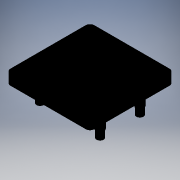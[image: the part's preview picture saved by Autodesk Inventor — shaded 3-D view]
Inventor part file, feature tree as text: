
AUTODESK INVENTOR PART (.ipt)
format: ipt  version: 2017.3 (Build 213256000, 256)  size: 133,632 bytes
history: native  units: mm (DEFAULTED — no unit token found)
features: other x7, sketch x3, extrude x2, revolve x1, pattern_linear x1
ambient origin geometry x8: Origin, YZ Plane, XZ Plane, XY Plane, X Axis, Y Axis, Z Axis, Center Point
bodies: Solid1 (feature_tree)
feature tree (14):
  extrude  "Extrusion1"  Depth=1.0mm TaperAngle=0.0deg
  extrude  "Extrusion2"  Depth=20.0mm
  revolve  "Revolution1"  [1 undecoded]
  pattern_linear  "Rectangular Pattern1"  [2 undecoded]
  other  "Cap_to_Frame_XY"
  other  "Cap_to_Frame_YZ"
  other  "Cap_to_Frame_ZX"
  other  "Cap_to_Frame_X"
  other  "Cap_to_Frame_Y"
  other  "Cap_to_Frame_Z"
  other  "Cap_to_Frame_Center"
  sketch  "Sketch_1"  dims[d0=2.5mm d1=0.0mm d2=1.0mm d3=0.0mm]
  sketch  "Sketch_2"  dims[d4=360.0deg d5=20.0mm d7=14.3mm d8=20.0mm d10=9.5mm]
  sketch  "Sketch_3"  dims[d11=0.0mm]
note: 3 required parameter values undecoded (feature->parameter linkage not recoverable at this tier; creation-order binding heuristic only, values carry confidence <= 0.55)
